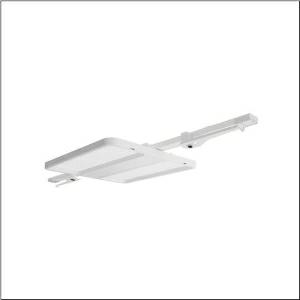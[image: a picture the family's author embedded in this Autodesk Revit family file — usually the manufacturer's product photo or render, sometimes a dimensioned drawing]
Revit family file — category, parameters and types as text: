
# Revit family: highbay_11_fur_modario_r__tragschiene_midi_51hn11da3fma_091e
name_source: partatom
category: Lighting Fixtures
units: mm (PartAtom-declared; Revit-internal decimal feet)

## family parameters
Cut with Voids When Loaded = No
Host = Face
Light Source = No
Part Type = Normal
Room Calculation Point = No
Round Connector Dimension = Use Diameter
Shared = No

## types (1)
- --- (1 x LED, 14260 lm, 73.2 W, 3000K)
    Apparent Load = 73 VA
    CIE Flux Codes = 85 97 100 100 100
    Color Rendering = 80
    Color Temperature = 3000K
    Default Elevation = 1800 mm
    Description = high bay luminaire Highbay 11 for Modario® trunking rail midi; direct symmetric narrow distribution, light control with lens of PMMA; UGR ≤ 22 (X = 4H | Y = 8H | S = 0.25H | reflection values 70/50/20); luminous flux: 14.260lm; light colour: 830, colour temperature: 3000K, MacAdam ≤ 2 SDCM (initial), colour rendering: CRI > 80; luminous efficacy: 194,8lm/W; rated service life: 100.000h (L95/B50) at AT= 25°C; control: DALI 2; luminaire connection: plug, 5-pole, with phase selectionmains connection: 230..240V, AC 50/60Hz; connected load: 73,2W; protection rating (complete): IP64; insulation class (complete): insulation class I (protective earthing); protection symbol: D; impact resistance: IK07; certification: CE, ENEC, VDE, UKCA; internal wiring halogen-free; luminaire corresponds to IFS (International Featured Standards) requirements for safety and quality in the food industry; LABS conformity tested according to VDMA 24364:2018-05; housing frame of high-performance plastic PA6, matt traffic white (RAL 9016); cover of PMMA; fixing on rail side of steel, galvanised, white; blank cover of PC, traffic white (RAL 9016); dimension (LxWxH): 1.195 x 442 x 72mm; permissible operating ambient temperature: -40..+55°C (reducing of maximum allowable ambient temperature of 5°C with ceiling mounting); packaging unit: 1 piece
    Height = 72 mm  [stored 0.23622 ft]
    Lamp = 1 x LED
    Lamp Light Flux = 14260 lm
    Lamp Power = 73.2 W
    Lamp count = 1
    Length = 474 mm
    Luminous efficacy = 195 lm/W
    Manufacturer = Siteco
    ModVariant = No
    Model = 51HN11DA3FMA
    Mounting Place = Ceiling
    Mounting Type = Pendant
    Number of Poles = 1
    OnlyDefault = Yes
    Power Factor = 1
    Product Name = Highbay 11 für Modario® Tragschiene midi
    Product group = high bay luminaire
    ProductGroupID = 901
    Protection Class = Protection class I
    Protection Degree = IP 64
    RLX_Detail_Level = 1
    RLX_Emergency_Light_Flux = 0 lm
    RLX_Emergency_Type = 0
    RLX_Emergency_Type_DB = No
    RlxData = <blob elided: 18145 chars, md5=07d0f654>
    Socket = socket
    Standby Power = 0 W
    System Light Flux = 14260 lm
    System Power = 73 W
    Type Comments = factory setting: luminous flux: 100 % | dim-lin: 254 | 339 mA
    Type Image = l_1363266.jpg
    URL = http://relux.com
    VarID = @adj_006101
    Voltage = 0 V
    Weight = 0.00 kg
    Width = 442 mm

note: [stored X ft] marks values corroborated as IEEE doubles in the binary element streams (Revit-internal decimal feet)

## geometry (parser evidence)
native form markers: Blend x4, Sweep x10
no freeform markers — native parametric forms only
